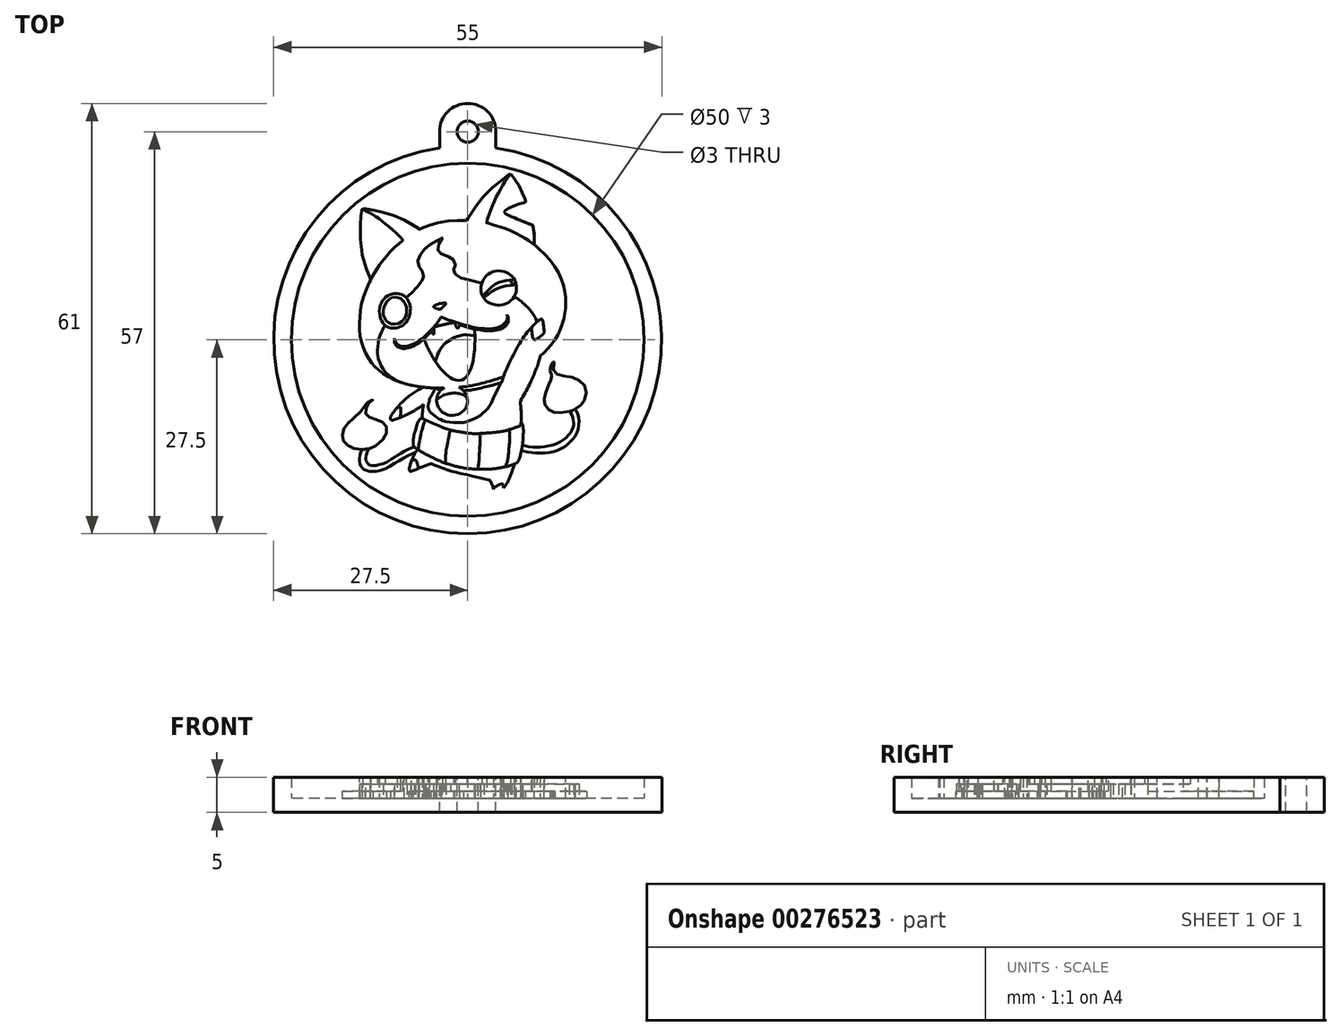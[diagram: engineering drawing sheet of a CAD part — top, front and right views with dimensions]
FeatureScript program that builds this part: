
annotation { "Feature Type Name" : "Feature", "Feature Type Description" : "" }
export const myFeature = defineFeature(function(context is Context, id is Id, definition is map)
    precondition{}
    {
        {
            var Q0;
            Q0=qCreatedBy(makeId("Top.planeOp"),FACE);
            var sketch = newSketch(context, id + "F0", { "sketchPlane" : qUnion([Q0])});
            skCircle(sketch, "E0", {"center": v(0, 0) * mm, "radius": 25 * mm});
            skCircle(sketch, "E1.0", {"center": v(0, 0) * mm, "radius": 27.5 * mm});
            skLineSegment(sketch, "E2", {"start": v(-4, 27.2) * mm, "end": v(-4, 29.5) * mm});
            skArc(sketch, "E3", {"start": v(4, 29.5) * mm, "mid": v(0, 33.5) * mm, "end": v(-4, 29.5) * mm});
            skLineSegment(sketch, "E4", {"start": v(4, 29.5) * mm, "end": v(4, 27.2) * mm});
            skCircle(sketch, "E5", {"center": v(0, 29.5) * mm, "radius": 1.5 * mm});
            skSolve(sketch);
        }
        {
            var Q0;
            Q0=qCreatedBy(makeId("Top.planeOp"),FACE);
            var sketch = newSketch(context, id + "F1", { "sketchPlane" : qUnion([Q0])});
            skFitSpline(sketch, "E6", {"points": [v(-14.9, 18.54) * mm, v(-10.75, 17.69) * mm, v(-6.9, 15.66) * mm, v(-6.92, 15.64) * mm, v(-3.9, 16.63) * mm, v(-0.22, 16.88) * mm, v(-0.17, 16.88) * mm, v(2, 20.03) * mm, v(6.07, 23.49) * mm, v(6.13, 23.46) * mm, v(7.33, 21.67) * mm, v(8.24, 19.6) * mm, v(8.25, 19.55) * mm, v(6.7, 19.01) * mm, v(5.3, 18.32) * mm, v(5.18, 18.16) * mm, v(5.27, 17.97) * mm, v(7.16, 17.05) * mm, v(9.16, 16.24) * mm, v(9.2, 16.22) * mm, v(9.42, 14.85) * mm, v(9.44, 13.5) * mm, v(9.45, 13.48) * mm, v(12.08, 10.75) * mm, v(13.87, 6.01) * mm, v(13.52, 2.62) * mm, v(11.9, -0.63) * mm, v(10.31, -2.27) * mm, v(10.28, -2.28) * mm, v(10.76, 0.32) * mm, v(10.58, 2.79) * mm, v(10.47, 2.93) * mm, v(10.22, 2.84) * mm, v(8.74, 1.45) * mm, v(6.26, -2.54) * mm, v(5.08, -5.24) * mm, v(5.07, -5.26) * mm, v(1.58, -6.27) * mm, v(-1.24, -6.73) * mm, v(-4.63, -6.85) * mm, v(-7.2, -6.6) * mm, v(-9.02, -6.22) * mm, v(-11.15, -5.32) * mm, v(-12.82, -4.16) * mm, v(-13.85, -2.95) * mm, v(-14.84, -0.97) * mm, v(-15.3, 0.87) * mm, v(-15.3, 3.25) * mm, v(-14.88, 5.78) * mm, v(-13.8, 8.44) * mm, v(-13.77, 8.48) * mm, v(-14.83, 11.57) * mm, v(-15.2, 15.11) * mm, v(-15.19, 16.95) * mm, v(-14.96, 18.46) * mm, v(-14.9, 18.54) * mm]});
            skFitSpline(sketch, "E7", {"points": [v(-13.77, 8.48) * mm, v(-13, 9.85) * mm, v(-12.12, 11.1) * mm, v(-10.97, 12.45) * mm, v(-9.2, 14.08) * mm, v(-9.17, 14.08) * mm, v(-10.44, 15.4) * mm, v(-11.77, 16.52) * mm, v(-13, 17.44) * mm, v(-14.9, 18.54) * mm], "startDerivative": vector(6.5, 12.03) * mm, "endDerivative": vector(-14.85, 8.04) * mm});
            skFitSpline(sketch, "E8", {"points": [v(9.45, 13.48) * mm, v(8.9, 13.86) * mm, v(8.05, 14.43) * mm, v(6.38, 15.33) * mm, v(4.2, 16.13) * mm, v(2.72, 16.55) * mm, v(2.68, 16.57) * mm, v(2.93, 17.52) * mm, v(3.5, 19.03) * mm, v(4.04, 20.24) * mm, v(4.65, 21.33) * mm, v(5.2, 22.26) * mm, v(6.07, 23.49) * mm], "startDerivative": vector(-8.4, 5.85) * mm, "endDerivative": vector(10.03, 13.4) * mm});
            skFitSpline(sketch, "E9", {"points": [v(-7.2, -6.6) * mm, v(-8.92, -6.2) * mm, v(-10.37, -5.63) * mm, v(-11.52, -4.72) * mm, v(-12.26, -3.68) * mm, v(-12.66, -2.64) * mm, v(-12.76, -1.99) * mm, v(-12.76, -1.05) * mm, v(-12.58, 0.1) * mm, v(-12.18, 1.17) * mm, v(-11.92, 1.69) * mm, v(-11.72, 2.02) * mm], "startDerivative": vector(-14.95, 3.15) * mm, "endDerivative": vector(3.7, 5.86) * mm});
            skFitSpline(sketch, "E10", {"points": [v(-11.72, 2.02) * mm, v(-11.94, 2.28) * mm, v(-12.2, 2.68) * mm, v(-12.38, 3.16) * mm, v(-12.51, 3.79) * mm, v(-12.48, 4.48) * mm, v(-12.2, 5.27) * mm, v(-11.9, 5.74) * mm, v(-11.45, 6.16) * mm, v(-10.97, 6.4) * mm, v(-10.35, 6.55) * mm, v(-9.78, 6.52) * mm, v(-9.27, 6.35) * mm, v(-8.92, 6.15) * mm, v(-8.71, 5.97) * mm, v(-8.55, 5.77) * mm, v(-8.3, 5.3) * mm, v(-8.14, 4.7) * mm, v(-8.17, 3.8) * mm, v(-8.41, 3) * mm, v(-8.84, 2.37) * mm, v(-9.37, 1.93) * mm, v(-10.06, 1.68) * mm, v(-10.6, 1.63) * mm, v(-11.1, 1.7) * mm, v(-11.72, 2.02) * mm]});
            skFitSpline(sketch, "E11", {"points": [v(2, 8.03) * mm, v(1.9, 7.6) * mm, v(1.89, 7) * mm, v(2.03, 6.39) * mm, v(2.36, 5.82) * mm, v(2.8, 5.38) * mm, v(3.36, 5.1) * mm, v(3.9, 4.94) * mm, v(4.6, 4.9) * mm, v(5.28, 5.06) * mm, v(5.93, 5.4) * mm, v(6.59, 6.09) * mm, v(6.87, 6.88) * mm, v(6.88, 7.68) * mm, v(6.67, 8.45) * mm, v(6.2, 9.08) * mm, v(5.7, 9.41) * mm, v(5.25, 9.63) * mm, v(4.4, 9.77) * mm, v(3.62, 9.64) * mm, v(2.88, 9.27) * mm, v(2.47, 8.88) * mm, v(2.19, 8.45) * mm, v(2, 8.03) * mm]});
            skFitSpline(sketch, "E12", {"points": [v(2.34, 6.4) * mm, v(2.77, 6.9) * mm, v(3.28, 7.4) * mm, v(4.05, 7.96) * mm, v(4.82, 8.27) * mm, v(5.47, 8.4) * mm, v(6.19, 8.47) * mm, v(6.25, 8.45) * mm, v(6.17, 8.38) * mm, v(6.07, 8.28) * mm, v(6.05, 8.24) * mm, v(6.08, 8.2) * mm, v(6.18, 8.14) * mm, v(6.37, 8) * mm, v(6.57, 7.8) * mm, v(6.58, 7.74) * mm, v(6.57, 7.74) * mm, v(6.28, 7.73) * mm, v(5.3, 7.6) * mm, v(4.13, 7.23) * mm, v(3.16, 6.66) * mm, v(2.55, 6.18) * mm, v(2.5, 6.14) * mm, v(2.46, 6.16) * mm, v(2.36, 6.27) * mm, v(2.34, 6.4) * mm]});
            skFitSpline(sketch, "E13", {"points": [v(-8.71, 5.97) * mm, v(-8.37, 6.27) * mm, v(-7.8, 6.81) * mm, v(-7.19, 7.5) * mm, v(-6.69, 8.09) * mm, v(-6.42, 8.47) * mm, v(-6.32, 8.63) * mm, v(-6.26, 9.01) * mm, v(-6.3, 9.38) * mm, v(-6.45, 9.71) * mm, v(-6.71, 10.09) * mm, v(-6.88, 10.37) * mm, v(-7.03, 10.78) * mm, v(-7.06, 11.18) * mm, v(-6.92, 11.62) * mm, v(-6.53, 12.26) * mm, v(-6.2, 12.72) * mm, v(-5.89, 13.04) * mm, v(-5.37, 13.48) * mm, v(-4.76, 13.85) * mm, v(-3.79, 14.38) * mm, v(-3.58, 14.48) * mm, v(-3.71, 14.25) * mm, v(-4.04, 13.69) * mm, v(-4.24, 13.2) * mm, v(-4.23, 12.67) * mm, v(-4.08, 12.48) * mm, v(-3.84, 12.26) * mm, v(-2.97, 11.92) * mm, v(-2.52, 11.68) * mm, v(-2.28, 11.55) * mm, v(-1.95, 11.25) * mm, v(-1.78, 10.83) * mm, v(-1.79, 10.46) * mm, v(-1.93, 10.07) * mm, v(-2, 9.85) * mm, v(-1.97, 9.6) * mm, v(-1.75, 9.3) * mm, v(-1.44, 9.02) * mm, v(-0.9, 8.74) * mm, v(0.63, 8.35) * mm, v(2, 8.03) * mm], "startDerivative": vector(14.21, 11.58) * mm, "endDerivative": vector(32.03, -7.9) * mm});
            skFitSpline(sketch, "E14", {"points": [v(9.83, 2.54) * mm, v(9.57, 3.1) * mm, v(9.14, 3.8) * mm, v(8.7, 4.37) * mm, v(7.95, 5.1) * mm, v(7.24, 5.7) * mm, v(6.59, 6.09) * mm], "startDerivative": vector(-1.62, 3.67) * mm, "endDerivative": vector(-4.07, 2.27) * mm});
            skFitSpline(sketch, "E15", {"points": [v(-10.3, 6.05) * mm, v(-10.02, 6.01) * mm, v(-9.5, 5.85) * mm, v(-8.99, 5.36) * mm, v(-8.74, 4.8) * mm, v(-8.64, 4.03) * mm, v(-8.83, 3.3) * mm, v(-9.18, 2.72) * mm, v(-9.84, 2.3) * mm, v(-10.53, 2.22) * mm, v(-11.02, 2.3) * mm, v(-11.42, 2.55) * mm, v(-11.73, 2.97) * mm, v(-11.91, 3.38) * mm, v(-11.98, 3.98) * mm, v(-11.84, 4.65) * mm, v(-11.62, 5.2) * mm, v(-11.25, 5.65) * mm, v(-10.83, 5.94) * mm, v(-10.3, 6.05) * mm]});
            skFitSpline(sketch, "E16", {"points": [v(-10.4, 0.11) * mm, v(-10.4, -0.18) * mm, v(-10.32, -0.51) * mm, v(-10.07, -0.88) * mm, v(-9.7, -1.1) * mm, v(-9.32, -1.21) * mm, v(-8.68, -1.21) * mm, v(-7.72, -0.93) * mm, v(-7.17, -0.63) * mm, v(-6.25, 0.1) * mm, v(-5.65, 0.68) * mm, v(-5.03, 1.35) * mm, v(-4.67, 1.82) * mm, v(-4.21, 2.4) * mm, v(-3.73, 3.1) * mm, v(-3.68, 3.2) * mm, v(-3.66, 3.19) * mm, v(-3.16, 2.94) * mm, v(-2.25, 2.54) * mm, v(-1.78, 2.37) * mm, v(-1.33, 2.2) * mm, v(-0.51, 1.92) * mm, v(0.36, 1.66) * mm, v(1.54, 1.4) * mm, v(2.54, 1.3) * mm, v(3.15, 1.26) * mm, v(4.06, 1.36) * mm, v(4.93, 1.63) * mm, v(5.5, 2.1) * mm, v(5.7, 2.39) * mm, v(5.75, 2.57) * mm, v(5.77, 2.98) * mm, v(5.71, 3.2) * mm, v(5.6, 3.45) * mm, v(5.53, 3.57) * mm, v(5.52, 3.57) * mm], "startDerivative": vector(-0.72, -13.54) * mm, "endDerivative": vector(-1.6, -0.63) * mm});
            skFitSpline(sketch, "E17", {"points": [v(-4.85, 4.74) * mm, v(-4.83, 4.77) * mm, v(-4.1, 5.1) * mm, v(-3.16, 5.2) * mm, v(-3.1, 5.16) * mm, v(-3.12, 5.09) * mm, v(-3.76, 4.4) * mm, v(-3.84, 4.33) * mm, v(-4.08, 4.33) * mm, v(-4.83, 4.66) * mm, v(-4.85, 4.74) * mm]});
            skFitSpline(sketch, "E18", {"points": [v(0.91, 1.52) * mm, v(0.98, 1.17) * mm, v(1.04, 0.17) * mm, v(0.93, -1.8) * mm, v(0.64, -3.53) * mm, v(0.22, -4.56) * mm, v(-0.07, -5.07) * mm, v(-0.14, -5.17) * mm, v(-0.34, -5.4) * mm, v(-0.86, -5.72) * mm, v(-1.63, -5.75) * mm, v(-2.3, -5.44) * mm, v(-2.68, -5.23) * mm, v(-3.42, -4.54) * mm, v(-4.2, -3.63) * mm, v(-5.2, -2.06) * mm, v(-6.1, -0.12) * mm, v(-6.18, 0.15) * mm, v(-6.19, 0.14) * mm], "startDerivative": vector(1.88, -8.5) * mm, "endDerivative": vector(-0.89, -1.31) * mm});
            skFitSpline(sketch, "E19", {"points": [v(-4.52, -3.18) * mm, v(-4.49, -2.83) * mm, v(-4.2, -1.93) * mm, v(-3.8, -1.2) * mm, v(-3.2, -0.54) * mm, v(-2.3, 0.1) * mm, v(-1.44, 0.46) * mm, v(-0.93, 0.63) * mm, v(-0.2, 0.73) * mm, v(1.03, 0.58) * mm, v(1.03, 0.59) * mm], "startDerivative": vector(0, 4.28) * mm, "endDerivative": vector(-0.45, 0.85) * mm});
            skFitSpline(sketch, "E20", {"points": [v(5.07, -5.26) * mm, v(4.92, -5.69) * mm, v(4.7, -6.4) * mm, v(4.54, -6.9) * mm], "startDerivative": vector(-0.49, -1.31) * mm, "endDerivative": vector(-0.47, -1.46) * mm});
            skFitSpline(sketch, "E21", {"points": [v(9.13, 1.87) * mm, v(9.07, 1.55) * mm, v(9.1, 1.04) * mm, v(9.17, 0.53) * mm, v(9.32, 0.1) * mm, v(9.4, 0.04) * mm, v(9.54, 0.04) * mm, v(9.94, 0.23) * mm, v(10.41, 0.55) * mm, v(10.8, 0.93) * mm], "startDerivative": vector(-0.7, -2.9) * mm, "endDerivative": vector(2.75, 2.95) * mm});
            skFitSpline(sketch, "E22", {"points": [v(10.28, -2.28) * mm, v(10.14, -2.78) * mm, v(9.94, -3.5) * mm, v(9.58, -4.44) * mm, v(8.88, -6.1) * mm, v(8.1, -7.58) * mm, v(7.32, -8.9) * mm], "startDerivative": vector(-1.17, -4.3) * mm, "endDerivative": vector(-4.07, -6.8) * mm});
            skFitSpline(sketch, "E23", {"points": [v(7.46, -8.67) * mm, v(7.48, -9.05) * mm, v(7.56, -10.05) * mm, v(7.58, -11.18) * mm, v(7.54, -12.08) * mm, v(7.53, -12.17) * mm, v(7.5, -12.18) * mm, v(5.81, -12.76) * mm, v(4.37, -13.06) * mm, v(1.72, -13.3) * mm, v(0.42, -13.28) * mm, v(-0.98, -13.09) * mm, v(-1.77, -12.96) * mm, v(-2.44, -12.8) * mm, v(-3.04, -12.61) * mm, v(-3.73, -12.35) * mm, v(-4.3, -12.1) * mm], "startDerivative": vector(0.28, -7.95) * mm, "endDerivative": vector(-10.19, 4.9) * mm});
            skFitSpline(sketch, "E24", {"points": [v(-6.2, -6.74) * mm, v(-6.73, -6.98) * mm, v(-7.4, -7.36) * mm, v(-8.26, -7.95) * mm, v(-8.97, -8.55) * mm, v(-9.5, -9.06) * mm, v(-9.97, -9.6) * mm, v(-10.67, -10.47) * mm, v(-10.92, -10.92) * mm, v(-10.97, -11.17) * mm, v(-10.93, -11.32) * mm, v(-10.78, -11.39) * mm, v(-10.47, -11.36) * mm, v(-9.54, -11) * mm, v(-8.98, -10.8) * mm], "startDerivative": vector(-7.39, -3.32) * mm, "endDerivative": vector(6.95, 2.44) * mm});
            skFitSpline(sketch, "E25", {"points": [v(-9.54, -11) * mm, v(-9.5, -9.68) * mm, v(-9.54, -9.6) * mm, v(-9.97, -9.6) * mm], "startDerivative": vector(0.16, 3.16) * mm, "endDerivative": vector(-1.77, -0.11) * mm});
            skFitSpline(sketch, "E26", {"points": [v(-4.49, -6.85) * mm, v(-4.73, -7.15) * mm, v(-5.13, -7.93) * mm, v(-5.44, -8.68) * mm, v(-4.4, -11) * mm, v(-4.02, -11.24) * mm, v(-3.85, -11.32) * mm, v(-3.48, -11.48) * mm, v(-2.77, -11.66) * mm, v(-2.05, -11.74) * mm, v(-1.3, -11.76) * mm, v(-0.5, -11.7) * mm, v(0.25, -11.5) * mm, v(1.01, -11.17) * mm, v(1.78, -10.72) * mm, v(2.3, -10.26) * mm, v(2.77, -9.78) * mm, v(3.13, -9.34) * mm, v(3.65, -8.27) * mm, v(4.7, -6.1) * mm, v(4.7, -6.1) * mm], "startDerivative": vector(-7.08, -8.58) * mm, "endDerivative": vector(-0.33, 0.6) * mm});
            skFitSpline(sketch, "E27", {"points": [v(-5.44, -8.68) * mm, v(-5.55, -9.04) * mm, v(-5.58, -9.2) * mm, v(-5.6, -9.36) * mm, v(-5.57, -9.72) * mm, v(-5.37, -10.18) * mm, v(-4.4, -11) * mm], "startDerivative": vector(-0.79, -2.52) * mm, "endDerivative": vector(3.94, -2.88) * mm});
            skFitSpline(sketch, "E28", {"points": [v(-5.13, -7.93) * mm, v(-5.32, -8.4) * mm, v(-5.44, -8.68) * mm], "startDerivative": vector(-0.37, -0.87) * mm, "endDerivative": vector(-0.24, -0.62) * mm});
            skFitSpline(sketch, "E29", {"points": [v(-4.49, -6.85) * mm, v(-4.28, -7) * mm, v(-4.06, -7.06) * mm, v(-3.78, -7.12) * mm], "startDerivative": vector(0.6, -0.5) * mm, "endDerivative": vector(0.82, -0.15) * mm});
            skFitSpline(sketch, "E30", {"points": [v(-3.3, -6.85) * mm, v(-3.6, -6.98) * mm, v(-3.78, -7.12) * mm], "startDerivative": vector(-0.6, -0.24) * mm, "endDerivative": vector(-0.34, -0.3) * mm});
            skFitSpline(sketch, "E31", {"points": [v(-3.78, -7.12) * mm, v(-3.92, -7.3) * mm, v(-4.12, -7.57) * mm, v(-4.25, -7.86) * mm, v(-4.36, -8.19) * mm, v(-4.4, -8.49) * mm, v(-4.4, -8.77) * mm, v(-4.3, -9.26) * mm, v(-4.05, -9.74) * mm, v(-3.71, -10.16) * mm, v(-3.37, -10.42) * mm, v(-2.87, -10.64) * mm, v(-2.58, -10.71) * mm, v(-2.2, -10.72) * mm, v(-1.75, -10.67) * mm, v(-1.11, -10.45) * mm, v(-0.38, -9.84) * mm, v(-0.05, -9.06) * mm, v(-0.03, -8.55) * mm, v(-0.17, -7.92) * mm, v(-0.59, -7.27) * mm, v(-0.94, -6.94) * mm, v(-1.24, -6.73) * mm], "startDerivative": vector(-4.36, -5.2) * mm, "endDerivative": vector(-7.38, 4.9) * mm});
            skFitSpline(sketch, "E32", {"points": [v(-4.4, -8.49) * mm, v(-3.93, -8.15) * mm, v(-3.47, -7.88) * mm, v(-2.82, -7.67) * mm, v(-2.25, -7.58) * mm, v(-1.7, -7.57) * mm, v(-1.18, -7.64) * mm, v(-0.76, -7.76) * mm, v(-0.4, -7.94) * mm, v(-0.23, -8.08) * mm, v(-0.06, -8.3) * mm], "startDerivative": vector(4.2, 3.16) * mm, "endDerivative": vector(2.2, -3.03) * mm});
            skFitSpline(sketch, "E33", {"points": [v(-0.62, -7.23) * mm, v(-0.1, -7.19) * mm, v(0.44, -7.13) * mm, v(1.04, -7.01) * mm, v(2.19, -6.76) * mm, v(3.32, -6.5) * mm, v(3.62, -6.44) * mm, v(4.1, -6.29) * mm, v(4.7, -6.1) * mm, v(4.8, -6.05) * mm, v(4.8, -6.05) * mm], "startDerivative": vector(4.87, 0.43) * mm, "endDerivative": vector(-0.01, 0.17) * mm});
            skFitSpline(sketch, "E34", {"points": [v(-8.98, -10.8) * mm, v(-7.45, -9.98) * mm, v(-6.2, -9.15) * mm], "startDerivative": vector(3.05, 1.56) * mm, "endDerivative": vector(2.51, 1.74) * mm});
            skFitSpline(sketch, "E35", {"points": [v(-6.27, -9.2) * mm, v(-6.43, -10.53) * mm, v(-6.44, -11.95) * mm], "startDerivative": vector(-0.39, -2.68) * mm, "endDerivative": vector(0.05, -2.82) * mm});
            skFitSpline(sketch, "E36", {"points": [v(-3.16, -17.5) * mm, v(-4.22, -17.08) * mm, v(-5.1, -16.65) * mm, v(-6.02, -16.19) * mm, v(-6.95, -15.63) * mm, v(-7.43, -15.33) * mm, v(-7.62, -15.18) * mm, v(-7.7, -14.63) * mm, v(-7.64, -13.74) * mm, v(-7.29, -12.38) * mm, v(-6.97, -11.5) * mm, v(-6.76, -11.23) * mm, v(-6.6, -11.12) * mm, v(-6.2, -11.27) * mm, v(-5.41, -11.65) * mm, v(-4.3, -12.1) * mm], "startDerivative": vector(-13.17, 4.95) * mm, "endDerivative": vector(13.68, -5.22) * mm});
            skFitSpline(sketch, "E37", {"points": [v(7.56, -11.7) * mm, v(7.66, -11.8) * mm, v(7.78, -12.06) * mm, v(7.87, -12.52) * mm, v(7.88, -13.3) * mm, v(7.8, -14.6) * mm, v(7.58, -15.86) * mm, v(7.34, -16.8) * mm, v(7.1, -17.3) * mm, v(7.06, -17.38) * mm, v(6.79, -17.53) * mm, v(6.05, -17.82) * mm, v(5.32, -18.02) * mm, v(4.03, -18.25) * mm, v(2.52, -18.36) * mm, v(1.34, -18.34) * mm, v(-0.21, -18.23) * mm, v(-1.83, -17.9) * mm, v(-3.16, -17.5) * mm], "startDerivative": vector(5.3, -3.85) * mm, "endDerivative": vector(-17.93, 5.58) * mm});
            skFitSpline(sketch, "E38", {"points": [v(5.81, -12.76) * mm, v(5.9, -13.1) * mm, v(5.95, -13.84) * mm, v(5.88, -15.01) * mm, v(5.81, -15.67) * mm, v(5.72, -16.68) * mm, v(5.67, -16.93) * mm, v(5.59, -17.31) * mm, v(5.52, -17.55) * mm, v(5.42, -17.82) * mm, v(5.32, -18.02) * mm], "startDerivative": vector(1.3, -3.61) * mm, "endDerivative": vector(-1.55, -2.83) * mm});
            skFitSpline(sketch, "E39", {"points": [v(1.72, -13.3) * mm, v(1.77, -13.43) * mm, v(1.78, -13.6) * mm, v(1.72, -14.72) * mm, v(1.63, -16.45) * mm, v(1.54, -17.68) * mm, v(1.47, -18.02) * mm, v(1.44, -18.21) * mm, v(1.34, -18.34) * mm], "startDerivative": vector(0.8, -2.1) * mm, "endDerivative": vector(-1.65, -1.6) * mm});
            skFitSpline(sketch, "E40", {"points": [v(-3.16, -17.5) * mm, v(-3.16, -17.28) * mm, v(-3.13, -16.4) * mm, v(-3, -15.39) * mm, v(-2.62, -13.45) * mm, v(-2.52, -13.06) * mm, v(-2.44, -12.8) * mm], "startDerivative": vector(-0.03, 1.9) * mm, "endDerivative": vector(0.83, 2.43) * mm});
            skFitSpline(sketch, "E41", {"points": [v(-5.96, -11.39) * mm, v(-6.04, -11.46) * mm, v(-6.13, -11.67) * mm, v(-6.6, -13.24) * mm, v(-7, -15.38) * mm, v(-6.98, -15.51) * mm, v(-6.98, -15.56) * mm, v(-6.9, -15.66) * mm], "startDerivative": vector(-1.16, -0.83) * mm, "endDerivative": vector(1.16, -1.37) * mm});
            skFitSpline(sketch, "E42", {"points": [v(6.64, -17.6) * mm, v(6.35, -18.45) * mm, v(6.02, -19.38) * mm, v(5.47, -20.47) * mm, v(4.83, -21.3) * mm, v(4.35, -21.87) * mm, v(4.1, -22) * mm, v(3.9, -21.83) * mm, v(3.56, -20.82) * mm, v(3.21, -20) * mm, v(3.19, -19.93) * mm, v(3.1, -19.89) * mm, v(-0.41, -19.08) * mm, v(-3.06, -18.38) * mm, v(-5.1, -17.61) * mm, v(-5.23, -17.58) * mm, v(-5.38, -17.62) * mm, v(-6.45, -18.03) * mm, v(-7.2, -18.33) * mm, v(-7.97, -18.64) * mm, v(-8.13, -18.69) * mm, v(-8.25, -18.57) * mm, v(-8.26, -18.17) * mm, v(-7.88, -16.95) * mm, v(-7.36, -15.93) * mm, v(-7.1, -15.54) * mm, v(-7.11, -15.53) * mm], "startDerivative": vector(-6.58, -19.45) * mm, "endDerivative": vector(-1.7, 0.27) * mm});
            skFitSpline(sketch, "E43", {"points": [v(-7.96, -17.14) * mm, v(-7.77, -17.08) * mm, v(-7.55, -17.02) * mm, v(-7.44, -17.03) * mm, v(-7.3, -17.13) * mm, v(-7.17, -17.46) * mm, v(-6.95, -18.24) * mm], "startDerivative": vector(1.27, 0.44) * mm, "endDerivative": vector(0.79, -2.97) * mm});
            skFitSpline(sketch, "E44", {"points": [v(3.68, -21.17) * mm, v(3.7, -21.06) * mm, v(3.82, -20.93) * mm, v(4.25, -20.65) * mm, v(4.74, -20.46) * mm, v(4.95, -20.47) * mm, v(5.04, -20.62) * mm, v(5.08, -20.76) * mm, v(5.07, -21) * mm, v(5.07, -21) * mm], "startDerivative": vector(0.05, 1.37) * mm, "endDerivative": vector(0.21, 0.42) * mm});
            skFitSpline(sketch, "E45", {"points": [v(-13.96, -15.44) * mm, v(-14.5, -15.52) * mm, v(-15.01, -15.53) * mm, v(-15.9, -15.43) * mm, v(-16.44, -15.3) * mm, v(-17.02, -15) * mm, v(-17.47, -14.55) * mm, v(-17.7, -14.2) * mm, v(-17.78, -13.79) * mm, v(-17.74, -13.35) * mm, v(-17.61, -12.81) * mm, v(-17.4, -12.3) * mm, v(-16.96, -11.88) * mm, v(-16.73, -11.63) * mm, v(-15.78, -10.74) * mm, v(-15.15, -10.15) * mm, v(-15.04, -10.05) * mm, v(-14.91, -9.85) * mm, v(-14.57, -9.3) * mm, v(-14.47, -9.16) * mm, v(-14.24, -8.92) * mm, v(-14.02, -8.72) * mm, v(-13.48, -8.5) * mm, v(-13.35, -8.4) * mm, v(-13.45, -8.55) * mm, v(-13.5, -8.58) * mm, v(-13.87, -8.78) * mm, v(-13.96, -8.89) * mm, v(-14.16, -9.21) * mm, v(-14.4, -9.68) * mm, v(-14.49, -10.12) * mm, v(-14.47, -10.45) * mm, v(-14.32, -10.73) * mm, v(-14.06, -10.93) * mm, v(-13.42, -11.19) * mm, v(-12.73, -11.4) * mm, v(-12.32, -11.52) * mm, v(-11.89, -11.84) * mm, v(-11.6, -12.2) * mm, v(-11.5, -12.52) * mm, v(-11.52, -13.16) * mm, v(-11.68, -13.63) * mm, v(-12.1, -14.26) * mm, v(-13, -15.02) * mm, v(-13.47, -15.28) * mm, v(-13.96, -15.44) * mm]});
            skFitSpline(sketch, "E46", {"points": [v(-14.96, -15.53) * mm, v(-15.06, -15.7) * mm, v(-15.2, -16.17) * mm, v(-15.27, -16.44) * mm, v(-15.35, -17) * mm, v(-15.3, -17.6) * mm, v(-15.12, -17.98) * mm, v(-14.9, -18.23) * mm, v(-14.44, -18.5) * mm, v(-13.95, -18.64) * mm, v(-13.23, -18.66) * mm, v(-12.19, -18.48) * mm, v(-11.65, -18.28) * mm, v(-9.98, -17.29) * mm, v(-8.4, -16.38) * mm, v(-7.36, -15.93) * mm], "startDerivative": vector(-2.75, -3.97) * mm, "endDerivative": vector(11.64, 4.6) * mm});
            skFitSpline(sketch, "E47", {"points": [v(-13.85, -15.4) * mm, v(-14.02, -15.54) * mm, v(-14.3, -16.15) * mm, v(-14.42, -16.68) * mm, v(-14.4, -17.12) * mm, v(-14.34, -17.29) * mm, v(-14.2, -17.51) * mm, v(-14, -17.73) * mm, v(-13.62, -17.84) * mm, v(-13.22, -17.83) * mm, v(-12.66, -17.75) * mm, v(-11.6, -17.39) * mm, v(-10.9, -17.01) * mm, v(-10.2, -16.55) * mm, v(-9.36, -16.02) * mm, v(-8.33, -15.47) * mm, v(-7.62, -15.18) * mm], "startDerivative": vector(-4.44, -2.15) * mm, "endDerivative": vector(9.28, 3.5) * mm});
            skFitSpline(sketch, "E48", {"points": [v(15.26, -9.81) * mm, v(15.88, -9.39) * mm, v(16.28, -9.05) * mm, v(16.57, -8.56) * mm, v(16.8, -7.76) * mm, v(16.78, -7) * mm, v(16.45, -6.32) * mm, v(15.83, -5.77) * mm, v(15.25, -5.45) * mm, v(14.23, -5.23) * mm, v(13.25, -5.05) * mm, v(12.73, -4.9) * mm, v(12.4, -4.7) * mm, v(12.16, -4.33) * mm, v(12.1, -3.82) * mm, v(12.3, -3.03) * mm, v(12.33, -2.99) * mm, v(12.26, -3.03) * mm, v(11.94, -3.38) * mm, v(11.83, -3.57) * mm, v(11.73, -3.81) * mm, v(11.66, -4.1) * mm, v(11.66, -4.48) * mm, v(11.76, -4.8) * mm, v(11.89, -5.09) * mm, v(11.88, -5.38) * mm, v(11.77, -5.7) * mm, v(11.7, -5.85) * mm, v(11.45, -6.4) * mm, v(11.06, -7.37) * mm, v(10.81, -8.25) * mm, v(10.8, -8.55) * mm, v(10.81, -8.89) * mm, v(11, -9.34) * mm, v(11.3, -9.74) * mm, v(11.72, -10.05) * mm, v(12.22, -10.26) * mm, v(12.47, -10.3) * mm, v(13.43, -10.3) * mm, v(14.4, -10.15) * mm, v(14.86, -10.01) * mm, v(15.26, -9.81) * mm]});
            skFitSpline(sketch, "E49", {"points": [v(14.4, -10.15) * mm, v(14.56, -10.33) * mm, v(14.81, -10.77) * mm, v(14.97, -11.34) * mm, v(15, -11.84) * mm, v(14.96, -12.25) * mm, v(14.75, -12.8) * mm, v(14.47, -13.27) * mm, v(13.88, -13.9) * mm, v(13.1, -14.46) * mm, v(12.06, -14.9) * mm, v(10.64, -15.17) * mm, v(9.75, -15.24) * mm, v(8.43, -15.1) * mm, v(7.75, -14.94) * mm], "startDerivative": vector(3.67, -3.9) * mm, "endDerivative": vector(-8.54, 2.47) * mm});
            skFitSpline(sketch, "E50", {"points": [v(7.6, -15.74) * mm, v(8.1, -15.86) * mm, v(9.08, -16) * mm, v(9.84, -16.07) * mm, v(11.14, -16.06) * mm, v(12.19, -15.85) * mm, v(13.17, -15.46) * mm, v(13.98, -14.98) * mm, v(14.62, -14.4) * mm, v(15, -13.94) * mm, v(15.43, -13.25) * mm, v(15.7, -12.36) * mm, v(15.76, -11.42) * mm, v(15.63, -10.63) * mm, v(15.42, -10.12) * mm, v(15.22, -9.83) * mm, v(15.22, -9.84) * mm, v(15.22, -9.84) * mm], "startDerivative": vector(8.56, -2.19) * mm, "endDerivative": vector(0.57, 0.4) * mm});
            skFitSpline(sketch, "E51", {"points": [v(-3.68, 3.2) * mm, v(-2.82, 2.84) * mm, v(-1.66, 2.47) * mm, v(-0.14, 2.01) * mm, v(1.4, 1.67) * mm, v(2.58, 1.56) * mm, v(3.13, 1.55) * mm, v(3.7, 1.6) * mm, v(4.5, 1.82) * mm, v(5.02, 2.1) * mm, v(5.37, 2.46) * mm, v(5.58, 2.79) * mm, v(5.65, 3.05) * mm, v(5.53, 3.57) * mm], "startDerivative": vector(9.87, -4.28) * mm, "endDerivative": vector(-3, 8.93) * mm});
            skFitSpline(sketch, "E52", {"points": [v(-3.68, 3.2) * mm, v(-3.73, 3.22) * mm, v(-3.76, 3.23) * mm, v(-3.78, 3.2) * mm, v(-4.01, 2.82) * mm, v(-4.96, 1.63) * mm, v(-5.85, 0.71) * mm, v(-6.6, 0.08) * mm, v(-7.05, -0.25) * mm, v(-7.59, -0.55) * mm, v(-8.15, -0.77) * mm, v(-8.68, -0.93) * mm, v(-9.16, -0.97) * mm, v(-9.58, -0.9) * mm, v(-9.92, -0.71) * mm, v(-10.11, -0.51) * mm, v(-10.3, -0.14) * mm, v(-10.36, 0.04) * mm, v(-10.38, 0.09) * mm, v(-10.4, 0.17) * mm], "startDerivative": vector(-2.74, 1.32) * mm, "endDerivative": vector(-0.5, 3.72) * mm});
            skFitSpline(sketch, "E53", {"points": [v(-10.4, 0.17) * mm, v(-10.4, 0.14) * mm, v(-10.4, 0.11) * mm], "startDerivative": vector(-0.01, -0.06) * mm, "endDerivative": vector(0, -0.05) * mm});
            skFitSpline(sketch, "E54", {"points": [v(-5.26, 1.09) * mm, v(-5.04, 0.93) * mm, v(-4.84, 0.8) * mm, v(-4.8, 0.78) * mm, v(-4.78, 0.83) * mm, v(-4.78, 1.68) * mm], "startDerivative": vector(0.97, -0.74) * mm, "endDerivative": vector(-0.06, 2.84) * mm});
            skFitSpline(sketch, "E55", {"points": [v(-4.67, 1.82) * mm, v(-3.97, 2) * mm, v(-3.4, 2.14) * mm, v(-2.68, 2.31) * mm, v(-1.93, 2.42) * mm], "startDerivative": vector(2.85, 0.78) * mm, "endDerivative": vector(2.87, 0.34) * mm});
            skFitSpline(sketch, "E56", {"points": [v(-1.84, 2.4) * mm, v(-1.71, 2.06) * mm, v(-1.5, 1.65) * mm, v(-1.44, 1.6) * mm, v(-1.38, 1.65) * mm, v(-1.21, 1.91) * mm, v(-1.15, 2.13) * mm], "startDerivative": vector(0.55, -1.42) * mm, "endDerivative": vector(0.26, 1.22) * mm});
            skSolve(sketch);
        }
        {
            var Q0;
            Q0=makeQuery(id+"F0.imprint","IMPRINT",FACE,{"disambiguationData":[TD([[makeQuery(id+"F0.imprint","IMPRINT",EDGE,{"derivedFrom":sQuery(id+"F0.wireOp",EDGE,"E0")}),-1.0]])]});
            var Q1;
            Q1=makeQuery(id+"F0.imprint","IMPRINT",FACE,{"disambiguationData":[TD([[makeQuery(id+"F0.imprint","IMPRINT",EDGE,{"derivedFrom":sQuery(id+"F0.wireOp",EDGE,"E0")}),1.0]])]});
            var Q2;
            {var subQ1=sQuery(id+"F0.wireOp",EDGE,"E2");Q2=makeQuery(id+"F0.imprint","IMPRINT",FACE,{"disambiguationData":[TD([[makeQuery(id+"F0.imprint","IMPRINT",EDGE,{"derivedFrom":subQ1}),-1.0]])]});}
            extrude(context, id + "F2", {"entities" : qUnion([Q0, Q1, Q2]), "oppositeDirection" : true, "depth" : 2 * mm});
        }
        {
            var Q0;
            {var subQ0=sQuery(id+"F1.wireOp",EDGE,"E38");Q0=makeQuery(id+"F1.imprint","IMPRINT",FACE,{"disambiguationData":[TD([[makeQuery(id+"F1.imprint","IMPRINT",EDGE,{"derivedFrom":subQ0}),-1.0]])]});}
            var Q1;
            Q1=makeQuery(id+"F1.imprint","IMPRINT",FACE,{"disambiguationData":[TD([[makeQuery(id+"F1.imprint","IMPRINT",EDGE,{"derivedFrom":sQuery(id+"F1.wireOp",EDGE,"E15")}),-1.0]])]});
            var Q2;
            Q2=makeQuery(id+"F1.imprint","IMPRINT",FACE,{"disambiguationData":[TD([[makeQuery(id+"F1.imprint","IMPRINT",EDGE,{"derivedFrom":sQuery(id+"F1.wireOp",EDGE,"E12")}),-1.0]])]});
            var Q3;
            {var subQ4=sQuery(id+"F1.wireOp",EDGE,"E40");Q3=makeQuery(id+"F1.imprint","IMPRINT",FACE,{"disambiguationData":[TD([[makeQuery(id+"F1.imprint","IMPRINT",EDGE,{"derivedFrom":subQ4}),1.0]])]});}
            var Q4;
            {var subQ19=sQuery(id+"F1.wireOp",EDGE,"E9");Q4=makeQuery(id+"F1.imprint","IMPRINT",FACE,{"disambiguationData":[TD([[makeQuery(id+"F1.imprint","IMPRINT",EDGE,{"derivedFrom":subQ19}),-1.0]])]});}
            var Q5;
            {var subQ1=sQuery(id+"F1.wireOp",EDGE,"E30");Q5=makeQuery(id+"F1.imprint","IMPRINT",FACE,{"disambiguationData":[TD([[makeQuery(id+"F1.imprint","IMPRINT",EDGE,{"derivedFrom":subQ1}),1.0]])]});}
            var Q6;
            {var subQ0=sQuery(id+"F1.wireOp",EDGE,"E46");Q6=makeQuery(id+"F1.imprint","IMPRINT",FACE,{"disambiguationData":[TD([[makeQuery(id+"F1.imprint","IMPRINT",EDGE,{"derivedFrom":subQ0}),1.0]])]});}
            var Q7;
            {var subQ0=sQuery(id+"F1.wireOp",EDGE,"E49");Q7=makeQuery(id+"F1.imprint","IMPRINT",FACE,{"disambiguationData":[TD([[makeQuery(id+"F1.imprint","IMPRINT",EDGE,{"derivedFrom":subQ0}),1.0]])]});}
            extrude(context, id + "F3", {"entities" : qUnion([Q0, Q1, Q2, Q3, Q4, Q5, Q6, Q7]), "operationType" : NewBodyOperationType.ADD, "depth" : 2 * mm});
        }
        {
            var Q0;
            {var subQ6=sQuery(id+"F1.wireOp",EDGE,"E7");Q0=makeQuery(id+"F1.imprint","IMPRINT",FACE,{"disambiguationData":[TD([[makeQuery(id+"F1.imprint","IMPRINT",EDGE,{"derivedFrom":subQ6}),-1.0]])]});}
            var Q1;
            {var subQ24=sQuery(id+"F1.wireOp",EDGE,"E21");Q1=makeQuery(id+"F1.imprint","IMPRINT",FACE,{"disambiguationData":[TD([[makeQuery(id+"F1.imprint","IMPRINT",EDGE,{"derivedFrom":subQ24}),-1.0]])]});}
            var Q2;
            {var subQ5=sQuery(id+"F1.wireOp",EDGE,"E43");Q2=makeQuery(id+"F1.imprint","IMPRINT",FACE,{"disambiguationData":[TD([[makeQuery(id+"F1.imprint","IMPRINT",EDGE,{"derivedFrom":subQ5}),1.0]])]});}
            var Q3;
            {var subQ0=sQuery(id+"F1.wireOp",EDGE,"E32");Q3=makeQuery(id+"F1.imprint","IMPRINT",FACE,{"disambiguationData":[TD([[makeQuery(id+"F1.imprint","IMPRINT",EDGE,{"derivedFrom":subQ0}),-1.0]])]});}
            extrude(context, id + "F4", {"entities" : qUnion([Q0, Q1, Q2, Q3]), "operationType" : NewBodyOperationType.ADD, "depth" : 3 * mm});
        }
        {
            var Q0;
            {var subQ0=sQuery(id+"F1.wireOp",EDGE,"E7");Q0=makeQuery(id+"F1.imprint","IMPRINT",FACE,{"disambiguationData":[TD([[makeQuery(id+"F1.imprint","IMPRINT",EDGE,{"derivedFrom":subQ0}),1.0]])]});}
            var Q1;
            {var subQ0=sQuery(id+"F1.wireOp",EDGE,"E45");var subQ1=makeQuery(id+"F1.imprint","INTERSECT",VERTEX,{"derivedFrom":[subQ0,sQuery(id+"F1.wireOp",EDGE,"E46")]});Q1=makeQuery(id+"F1.imprint","IMPRINT",FACE,{"disambiguationData":[TD([[makeQuery(id+"F1.imprint","IMPRINT",EDGE,{"disambiguationData":[TD([[subQ1,-1.0]])],"derivedFrom":subQ0}),-1.0]])]});}
            var Q2;
            {var subQ0=sQuery(id+"F1.wireOp",EDGE,"E25");Q2=makeQuery(id+"F1.imprint","IMPRINT",FACE,{"disambiguationData":[TD([[makeQuery(id+"F1.imprint","IMPRINT",EDGE,{"derivedFrom":subQ0}),1.0]])]});}
            var Q3;
            {var subQ6=sQuery(id+"F1.wireOp",EDGE,"E38");Q3=makeQuery(id+"F1.imprint","IMPRINT",FACE,{"disambiguationData":[TD([[makeQuery(id+"F1.imprint","IMPRINT",EDGE,{"derivedFrom":subQ6}),1.0]])]});}
            var Q4;
            {var subQ0=sQuery(id+"F1.wireOp",EDGE,"E39");Q4=makeQuery(id+"F1.imprint","IMPRINT",FACE,{"disambiguationData":[TD([[makeQuery(id+"F1.imprint","IMPRINT",EDGE,{"derivedFrom":subQ0}),-1.0]])]});}
            var Q5;
            {var subQ0=sQuery(id+"F1.wireOp",EDGE,"E43");Q5=makeQuery(id+"F1.imprint","IMPRINT",FACE,{"disambiguationData":[TD([[makeQuery(id+"F1.imprint","IMPRINT",EDGE,{"derivedFrom":subQ0}),-1.0]])]});}
            var Q6;
            {var subQ0=sQuery(id+"F1.wireOp",EDGE,"E44");var subQ1=sQuery(id+"F1.wireOp",EDGE,"E42");var subQ2=makeQuery(id+"F1.imprint","INTERSECT",VERTEX,{"disambiguationData":[OD(0.0)],"derivedFrom":[subQ1,subQ0]});Q6=makeQuery(id+"F1.imprint","IMPRINT",FACE,{"disambiguationData":[TD([[makeQuery(id+"F1.imprint","IMPRINT",EDGE,{"disambiguationData":[TD([[subQ2,1.0]])],"derivedFrom":subQ1}),-1.0]])]});}
            var Q7;
            {var subQ2=sQuery(id+"F1.wireOp",EDGE,"E21");Q7=makeQuery(id+"F1.imprint","IMPRINT",FACE,{"disambiguationData":[TD([[makeQuery(id+"F1.imprint","IMPRINT",EDGE,{"derivedFrom":subQ2}),1.0]])]});}
            var Q8;
            {var subQ0=sQuery(id+"F1.wireOp",EDGE,"E8");Q8=makeQuery(id+"F1.imprint","IMPRINT",FACE,{"disambiguationData":[TD([[makeQuery(id+"F1.imprint","IMPRINT",EDGE,{"derivedFrom":subQ0}),-1.0]])]});}
            var Q9;
            {var subQ3=sQuery(id+"F1.wireOp",EDGE,"E30");Q9=makeQuery(id+"F1.imprint","IMPRINT",FACE,{"disambiguationData":[TD([[makeQuery(id+"F1.imprint","IMPRINT",EDGE,{"derivedFrom":subQ3}),1.0]])]});}
            var Q10;
            {var subQ4=sQuery(id+"F1.wireOp",EDGE,"E20");var subQ5=sQuery(id+"F1.wireOp",EDGE,"E6");var subQ6=makeQuery(id+"F1.imprint","INTERSECT",VERTEX,{"derivedFrom":[subQ5,subQ4]});Q10=makeQuery(id+"F1.imprint","IMPRINT",FACE,{"disambiguationData":[TD([[makeQuery(id+"F1.imprint","IMPRINT",EDGE,{"disambiguationData":[TD([[subQ6,-1.0]])],"derivedFrom":subQ5}),1.0]])]});}
            var Q11;
            {var subQ0=sQuery(id+"F1.wireOp",EDGE,"E29");Q11=makeQuery(id+"F1.imprint","IMPRINT",FACE,{"disambiguationData":[TD([[makeQuery(id+"F1.imprint","IMPRINT",EDGE,{"derivedFrom":subQ0}),1.0]])]});}
            extrude(context, id + "F5", {"entities" : qUnion([Q0, Q1, Q2, Q3, Q4, Q5, Q6, Q7, Q8, Q9, Q10, Q11]), "operationType" : NewBodyOperationType.ADD, "depth" : 1 * mm});
        }
        {
            var Q0;
            Q0=makeQuery(id+"F0.imprint","IMPRINT",FACE,{"disambiguationData":[TD([[makeQuery(id+"F0.imprint","IMPRINT",EDGE,{"derivedFrom":sQuery(id+"F0.wireOp",EDGE,"E0")}),-1.0]])]});
            var Q1;
            {var subQ1=sQuery(id+"F0.wireOp",EDGE,"E2");Q1=makeQuery(id+"F0.imprint","IMPRINT",FACE,{"disambiguationData":[TD([[makeQuery(id+"F0.imprint","IMPRINT",EDGE,{"derivedFrom":subQ1}),-1.0]])]});}
            extrude(context, id + "F6", {"entities" : qUnion([Q0, Q1]), "operationType" : NewBodyOperationType.ADD, "depth" : 3 * mm});
        }
        {
            var Q0;
            {var subQ9=sQuery(id+"F1.wireOp",EDGE,"E54");Q0=makeQuery(id+"F1.imprint","IMPRINT",FACE,{"disambiguationData":[TD([[makeQuery(id+"F1.imprint","IMPRINT",EDGE,{"derivedFrom":subQ9}),-1.0]])]});}
            var Q1;
            {var subQ0=sQuery(id+"F1.wireOp",EDGE,"E48");var subQ1=makeQuery(id+"F1.imprint","INTERSECT",VERTEX,{"derivedFrom":[subQ0,sQuery(id+"F1.wireOp",EDGE,"E49")]});Q1=makeQuery(id+"F1.imprint","IMPRINT",FACE,{"disambiguationData":[TD([[makeQuery(id+"F1.imprint","IMPRINT",EDGE,{"disambiguationData":[TD([[subQ1,-1.0]])],"derivedFrom":subQ0}),1.0]])]});}
            var Q2;
            {var subQ2=sQuery(id+"F1.wireOp",EDGE,"E41");Q2=makeQuery(id+"F1.imprint","IMPRINT",FACE,{"disambiguationData":[TD([[makeQuery(id+"F1.imprint","IMPRINT",EDGE,{"derivedFrom":subQ2}),-1.0]])]});}
            extrude(context, id + "F7", {"entities" : qUnion([Q0, Q1, Q2]), "depth" : 1 * mm});
        }
    });
